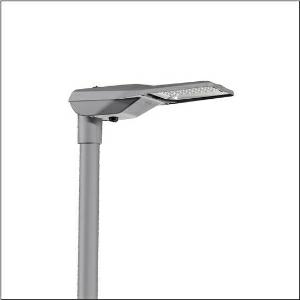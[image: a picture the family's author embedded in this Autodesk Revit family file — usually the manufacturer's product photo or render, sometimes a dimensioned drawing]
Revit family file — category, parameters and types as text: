
# Revit family: streetlight_sl_21_mini___stw1_0a_5xe2e33t08hb_df53
name_source: partatom
category: Lighting Fixtures
units: mm (PartAtom-declared; Revit-internal decimal feet)

## family parameters
Cut with Voids When Loaded = No
Host = Face
Light Source = No
Part Type = Normal
Room Calculation Point = No
Round Connector Dimension = Use Diameter
Shared = No

## types (1)
- --- (1 x LED, 9040 lm, 66 W, 3000K)
    Apparent Load = 66 VA
    CIE Flux Codes = 38 75 98 100 100
    Color Rendering = 70
    Color Temperature = 3000K
    Default Elevation = 1800 mm
    Description = Streetlight SL 21 mini, mast luminaire, primary light control with lens, of PMMA, primary optical cover: cover, of toughened safety glass, transparent, light distribution: STW1.0a, light emission: direct distribution, primary light characteristic: asymmetric, installation type: side-entry, post-top, LED, High Power LED, rated luminous flux: 9.040lm, luminous efficacy: 137lm/W, light colour: 730, colour temperature: 3000K, control gear: D4i, control: overheat protection, constant luminous flux control, time-dependent luminous flux control, flexible luminous flux parameterisation, pre-setting: logarithmic dimming characteristic, mains connection: 220..240V, AC, 50/60Hz, start of lifetime: 66W, end of service life: 69W, reduction: 30W, luminaire housing, of diecast aluminium, powder-coated, Siteco® metallic grey (DB 702S), corrosivity category C5 mid according to DIN EN ISO 12944, please order mast flange separately, inclination adjustable: 0°, 5°, 10°, 15°, sealing non-destructively replaceable, multi-level sealing system, length: 628mm, width: 235mm, height: 110mm, mast flange for spigot size: 42mm (side-entry): 5XC10008XM4, 60/48mm (side-entry/post-top): 5XC10108XM2, 76/60mm (side-entry/post-top): 5XC10108XM1, mounting height: 4..8m, Smart Interface below and above, protection rating (complete): IP66, insulation class (complete): insulation class II (safety insulation), certification: CE, ENEC, ENEC+, VDE, impact resistance: IK10, permissible operating ambient temperature for outdoor applications: -40..+50°C, standard-compliant lighting for roads and squares, packaging unit: 1 piece

Light Distribution: STW1.0a
    Height = 110 mm
    Lamp = 1 x LED
    Lamp Light Flux = 9040 lm
    Lamp Power = 66 W
    Lamp count = 1
    Length = 625 mm
    Luminous efficacy = 137 lm/W
    Manufacturer = Siteco
    ModVariant = No
    Model = 5XE2E33T08HB
    Number of Poles = 1
    OnlyDefault = Yes
    Power Factor = 1
    Product Name = Streetlight SL 21 mini | STW1.0a
    Product group = mast luminaire | pylon top
    ProductGroupID = 6100
    Protection Class = Protection class II
    Protection Degree = IP 66
    RLX_Detail_Level = 1
    RLX_Emergency_Light_Flux = 0 lm
    RLX_Emergency_Type = 0
    RLX_Emergency_Type_DB = No
    RlxData = <blob elided: 26313 chars, md5=6fac54cb>
    Socket = socket
    Standby Power = 0 W
    System Light Flux = 9040 lm
    System Power = 66 W
    Type Comments = factory setting: luminous flux: 100 % | dim-lin: 254 | 670 mA
    Type Image = l_1003514.jpg
    URL = http://relux.com
    VarID = @adj_208487
    Voltage = 0 V
    Weight = 0.00 kg
    Width = 234 mm

## geometry (parser evidence)
native form markers: Blend x4, Sweep x11
no freeform markers — native parametric forms only
